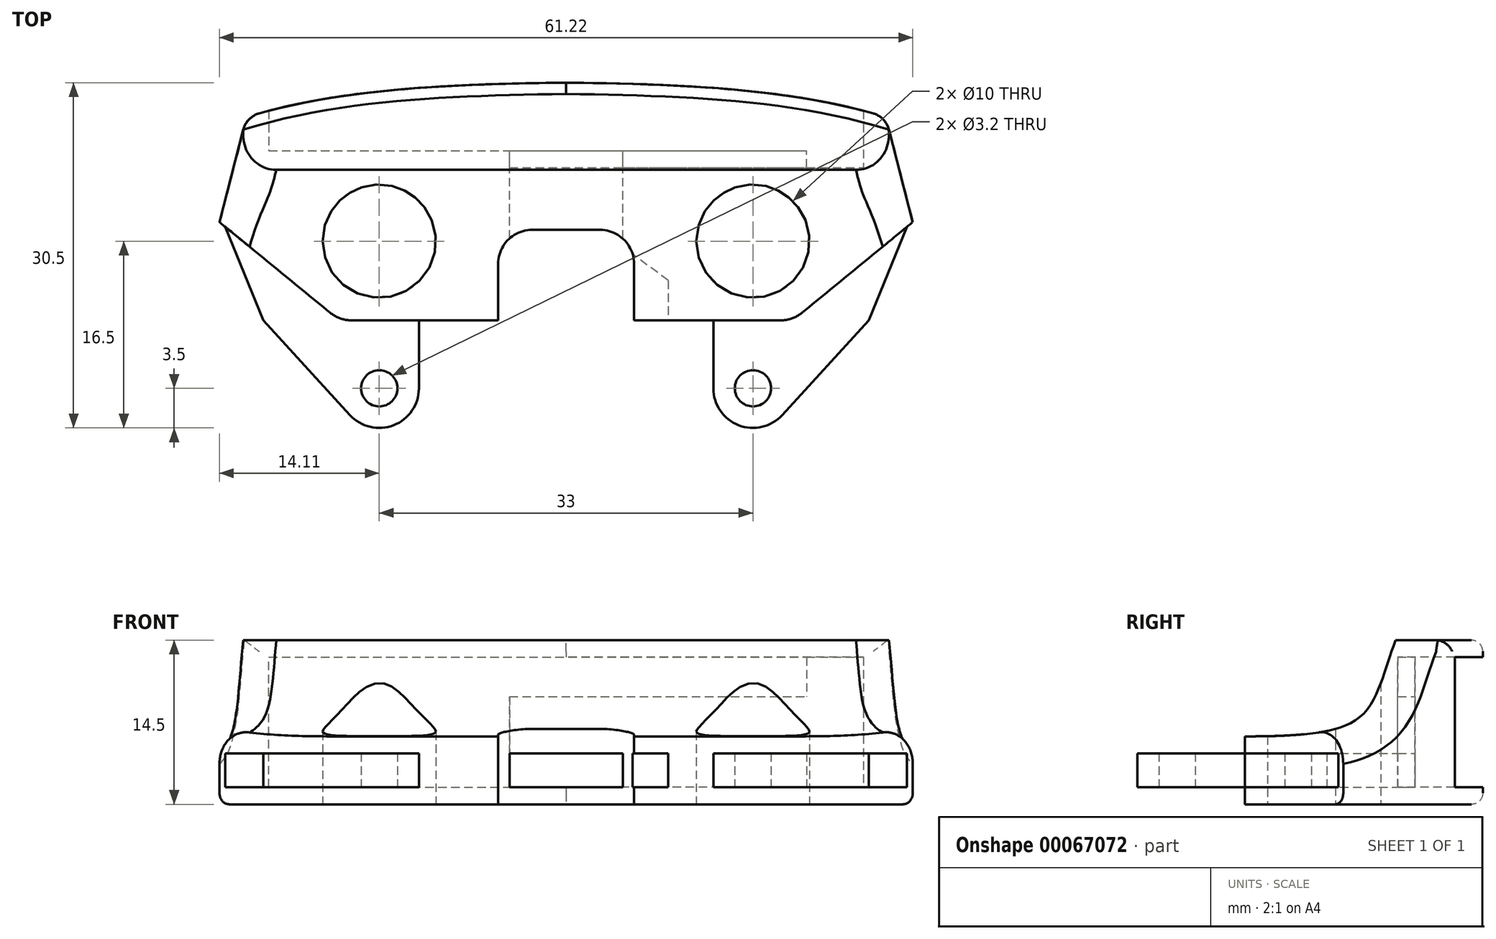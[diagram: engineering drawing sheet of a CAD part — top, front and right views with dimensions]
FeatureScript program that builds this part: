
annotation { "Feature Type Name" : "Feature", "Feature Type Description" : "" }
export const myFeature = defineFeature(function(context is Context, id is Id, definition is map)
    precondition{}
    {
        {
            var Q0;
            Q0=qCreatedBy(makeId("Top.planeOp"),FACE);
            var sketch = newSketch(context, id + "F0", { "sketchPlane" : qUnion([Q0])});
            skLineSegment(sketch, "E0", {"start": v(0, 0) * mm, "end": v(-18.93, 0) * mm});
            skLineSegment(sketch, "E1", {"start": v(-20.83, 0.68) * mm, "end": v(-30.6, 8.68) * mm});
            skLineSegment(sketch, "E2", {"start": v(-30.6, 8.68) * mm, "end": v(-28.5, 16.87) * mm});
            skCircle(sketch, "E3", {"center": v(-16.5, 7) * mm, "radius": 5 * mm});
            skCircle(sketch, "E4", {"center": v(-16.5, -6) * mm, "radius": 1.6 * mm});
            skLineSegment(sketch, "E5", {"start": v(-30.1, 8.26) * mm, "end": v(-26.74, 0) * mm});
            skArc(sketch, "E6", {"start": v(-19.08, -8.36) * mm, "mid": v(-15.23, -9.26) * mm, "end": v(-13, -6) * mm});
            skLineSegment(sketch, "E7", {"start": v(-26.74, 0) * mm, "end": v(-19.08, -8.36) * mm});
            skLineSegment(sketch, "E8", {"start": v(-13, 0) * mm, "end": v(-13, -6) * mm});
            skPoint(sketch, "E9.visualSharp", {"position": v(-20, 0) * mm});
            skArc(sketch, "E9.filletArc", {"start": v(-20.83, 0.68) * mm, "mid": v(-19.94, 0.17) * mm, "end": v(-18.93, 0) * mm});
            skFitSpline(sketch, "E10", {"points": [v(-28.22, 17.97) * mm, v(0, 21) * mm], "startDerivative": vector(21.2, 6.41) * mm, "endDerivative": vector(39.56, 0.4) * mm});
            skArc(sketch, "E11.filletArc", {"start": v(-27.1, 18.3) * mm, "mid": v(-28, 17.77) * mm, "end": v(-28.5, 16.87) * mm});
            skLineSegment(sketch, "E12.MirrorCS", {"start": v(0, 0) * mm, "end": v(18.93, 0) * mm});
            skLineSegment(sketch, "E13.MirrorCS", {"start": v(13, 0) * mm, "end": v(13, -6) * mm});
            skArc(sketch, "E14.MirrorCS", {"start": v(19.08, -8.36) * mm, "mid": v(15.23, -9.26) * mm, "end": v(13, -6) * mm});
            skCircle(sketch, "E15.MirrorC", {"center": v(16.5, -6) * mm, "radius": 1.6 * mm});
            skLineSegment(sketch, "E16.MirrorCS", {"start": v(26.74, 0) * mm, "end": v(19.08, -8.36) * mm});
            skLineSegment(sketch, "E17.MirrorCS", {"start": v(30.1, 8.26) * mm, "end": v(26.74, 0) * mm});
            skArc(sketch, "E18.MirrorCS", {"start": v(20.83, 0.68) * mm, "mid": v(19.94, 0.17) * mm, "end": v(18.93, 0) * mm});
            skLineSegment(sketch, "E19.MirrorCS", {"start": v(20.83, 0.68) * mm, "end": v(30.6, 8.68) * mm});
            skCircle(sketch, "E20.MirrorC", {"center": v(16.5, 7) * mm, "radius": 5 * mm});
            skLineSegment(sketch, "E21.MirrorCS", {"start": v(30.6, 8.68) * mm, "end": v(28.5, 16.87) * mm});
            skArc(sketch, "E22.MirrorCS", {"start": v(27.1, 18.3) * mm, "mid": v(28, 17.77) * mm, "end": v(28.5, 16.87) * mm});
            skFitSpline(sketch, "E23.MirrorCS", {"points": [v(28.22, 17.97) * mm, v(0, 21) * mm], "startDerivative": vector(-21.2, 6.41) * mm, "endDerivative": vector(-39.56, 0.4) * mm});
            skSolve(sketch);
        }
        {
            var Q0;
            {var subQ6=sQuery(id+"F0.wireOp",EDGE,"E2");Q0=makeQuery(id+"F0.imprint","IMPRINT",FACE,{"disambiguationData":[TD([[makeQuery(id+"F0.imprint","IMPRINT",EDGE,{"derivedFrom":subQ6}),-1.0]])]});}
            extrude(context, id + "F1", {"entities" : qUnion([Q0]), "depth" : 14.5 * mm});
        }
        {
            var Q0;
            Q0=makeQuery(id+"F0.imprint","IMPRINT",FACE,{"disambiguationData":[TD([[makeQuery(id+"F0.imprint","IMPRINT",EDGE,{"derivedFrom":sQuery(id+"F0.wireOp",EDGE,"E4")}),-1.0]])]});
            var Q1;
            {var subQ0=sQuery(id+"F0.wireOp",EDGE,"E13.MirrorCS");Q1=makeQuery(id+"F0.imprint","IMPRINT",FACE,{"disambiguationData":[TD([[makeQuery(id+"F0.imprint","IMPRINT",EDGE,{"derivedFrom":subQ0}),1.0]])]});}
            extrude(context, id + "F2", {"entities" : qUnion([Q0, Q1]), "operationType" : NewBodyOperationType.ADD, "depth" : 4.5 * mm, "hasSecondDirection" : true, "secondDirectionOppositeDirection" : false, "secondDirectionDepth" : 1.5 * mm});
        }
        {
            var Q0;
            Q0=qCreatedBy(makeId("Right.planeOp"),FACE);
            var sketch = newSketch(context, id + "F3", { "sketchPlane" : qUnion([Q0])});
            skLineSegment(sketch, "E24", {"start": v(18.3, 14.5) * mm, "end": v(13.3, 14.5) * mm});
            skFitSpline(sketch, "E25", {"points": [v(13.3, 14.5) * mm, v(0, 6) * mm], "startDerivative": vector(-7.24, -20.2) * mm, "endDerivative": vector(-35.3, 0) * mm});
            skLineSegment(sketch, "E26", {"start": v(18.3, 14.5) * mm, "end": v(18.3, 15.71) * mm});
            skLineSegment(sketch, "E27", {"start": v(18.3, 15.71) * mm, "end": v(0, 15.71) * mm});
            skLineSegment(sketch, "E28", {"start": v(0, 15.71) * mm, "end": v(0, 6) * mm});
            skLineSegment(sketch, "E29", {"start": v(0, 4.5) * mm, "end": v(0, 6) * mm, "construction": true});
            skLineSegment(sketch, "E30", {"start": v(21.02, 0) * mm, "end": v(21.02, 6) * mm, "construction": true});
            skSolve(sketch);
        }
        {
            var Q0;
            Q0=makeQuery(id+"F3.imprint","IMPRINT",FACE,{"disambiguationData":[TD([[makeQuery(id+"F3.imprint","IMPRINT",EDGE,{"derivedFrom":sQuery(id+"F3.wireOp",EDGE,"E24")}),-1.0]])]});
            extrude(context, id + "F4", {"entities" : qUnion([Q0]), "operationType" : NewBodyOperationType.REMOVE, "endBound" : BoundingType.SYMMETRIC, "oppositeDirection" : true, "depth" : 80 * mm});
        }
        {
            var Q0;
            Q0=qCreatedBy(makeId("Front.planeOp"),FACE);
            var sketch = newSketch(context, id + "F5", { "sketchPlane" : qUnion([Q0])});
            skLineSegment(sketch, "E31", {"start": v(0, 0) * mm, "end": v(0, 14.5) * mm, "construction": true});
            skLineSegment(sketch, "E32.rect.bottom", {"start": v(-26.25, 1.5) * mm, "end": v(26.25, 1.5) * mm});
            skLineSegment(sketch, "E32.rect.top", {"start": v(-26.25, 13) * mm, "end": v(26.25, 13) * mm});
            skLineSegment(sketch, "E32.rect.left", {"start": v(-26.25, 1.5) * mm, "end": v(-26.25, 13) * mm});
            skLineSegment(sketch, "E32.rect.right", {"start": v(26.25, 1.5) * mm, "end": v(26.25, 13) * mm});
            skPoint(sketch, "E32.rect.middle", {"position": v(0, 7.25) * mm});
            skSolve(sketch);
        }
        {
            var Q0;
            Q0=makeQuery(id+"F5.imprint","IMPRINT",FACE,{"disambiguationData":[TD([[makeQuery(id+"F5.imprint","IMPRINT",EDGE,{"derivedFrom":sQuery(id+"F5.wireOp",EDGE,"E32.rect.bottom")}),1.0]])]});
            extrude(context, id + "F6", {"entities" : qUnion([Q0]), "operationType" : NewBodyOperationType.REMOVE, "oppositeDirection" : true, "depth" : 25 * mm, "hasSecondDirection" : true, "secondDirectionOppositeDirection" : true, "secondDirectionDepth" : 15 * mm});
        }
        {
            var Q0;
            Q0=makeQuery(id+"F6.boolean.opBoolean","COPY",FACE,{"derivedFrom":makeQuery(id+"F6.opExtrude","CAP_FACE",FACE,{"disambiguationData":[OSD([sQuery(id+"F5.wireOp",EDGE,"E32.rect.bottom"),sQuery(id+"F5.wireOp",EDGE,"E32.rect.top"),sQuery(id+"F5.wireOp",EDGE,"E32.rect.left"),sQuery(id+"F5.wireOp",EDGE,"E32.rect.right")])],"isStart":true})});
            var sketch = newSketch(context, id + "F7", { "sketchPlane" : qUnion([Q0])});
            skLineSegment(sketch, "E33", {"start": v(0, 1.5) * mm, "end": v(-5, 1.5) * mm});
            skLineSegment(sketch, "E34", {"start": v(-5, 1.5) * mm, "end": v(-5, 4.5) * mm});
            skLineSegment(sketch, "E35", {"start": v(-5, 4.5) * mm, "end": v(5, 4.5) * mm});
            skLineSegment(sketch, "E36", {"start": v(5, 4.5) * mm, "end": v(5, 1.5) * mm});
            skLineSegment(sketch, "E37", {"start": v(5, 1.5) * mm, "end": v(0, 1.5) * mm});
            skSolve(sketch);
        }
        {
            var Q0;
            Q0=makeQuery(id+"F7.imprint","IMPRINT",FACE,{"disambiguationData":[TD([[makeQuery(id+"F7.imprint","IMPRINT",EDGE,{"derivedFrom":sQuery(id+"F7.wireOp",EDGE,"E33")}),-1.0]])]});
            extrude(context, id + "F8", {"entities" : qUnion([Q0]), "operationType" : NewBodyOperationType.REMOVE, "oppositeDirection" : true, "depth" : 25 * mm});
        }
        {
            var Q0;
            Q0=makeQuery(id+"F6.boolean.opBoolean","COPY",FACE,{"derivedFrom":makeQuery(id+"F6.opExtrude","CAP_FACE",FACE,{"disambiguationData":[OSD([sQuery(id+"F5.wireOp",EDGE,"E32.rect.bottom"),sQuery(id+"F5.wireOp",EDGE,"E32.rect.top"),sQuery(id+"F5.wireOp",EDGE,"E32.rect.left"),sQuery(id+"F5.wireOp",EDGE,"E32.rect.right")])],"isStart":true})});
            var sketch = newSketch(context, id + "F9", { "sketchPlane" : qUnion([Q0])});
            skLineSegment(sketch, "E38", {"start": v(-21.25, 13) * mm, "end": v(-21.25, 1.5) * mm});
            skLineSegment(sketch, "E39", {"start": v(-5, 4.5) * mm, "end": v(-21.25, 4.5) * mm});
            skLineSegment(sketch, "E40", {"start": v(5, 4.5) * mm, "end": v(5, 9.5) * mm});
            skLineSegment(sketch, "E41", {"start": v(5, 9.5) * mm, "end": v(-21.25, 9.5) * mm});
            skSolve(sketch);
        }
        {
            var Q0;
            {var subQ0=sQuery(id+"F5.wireOp",EDGE,"E32.rect.right");var subQ1=makeQuery(id+"F6.boolean.opBoolean","COPY",EDGE,{"derivedFrom":makeQuery(id+"F6.opExtrude","CAP_EDGE",EDGE,{"disambiguationData":[OSD([subQ0])],"isStart":true})});Q0=makeQuery(id+"F9.imprint","IMPRINT",FACE,{"disambiguationData":[TD([[makeQuery(id+"F9.imprint","IMPRINT",EDGE,{"derivedFrom":subQ1}),-1.0]])]});}
            var Q1;
            {var subQ0=sQuery(id+"F9.wireOp",EDGE,"E39");Q1=makeQuery(id+"F9.imprint","IMPRINT",FACE,{"disambiguationData":[TD([[makeQuery(id+"F9.imprint","IMPRINT",EDGE,{"derivedFrom":subQ0}),-1.0]])]});}
            extrude(context, id + "F10", {"entities" : qUnion([Q0, Q1]), "operationType" : NewBodyOperationType.REMOVE, "oppositeDirection" : true, "depth" : 1.5 * mm});
        }
        {
            var Q0;
            Q0=makeQuery(id+"F4.boolean.opBoolean","INTERSECT",EDGE,{"derivedFrom":[makeQuery(id+"F1.opExtrude","SWEPT_FACE",FACE,{"disambiguationData":[OSD([sQuery(id+"F0.wireOp",EDGE,"E2")])]}),makeQuery(id+"F4.opExtrude","SWEPT_FACE",FACE,{"disambiguationData":[OSD([sQuery(id+"F3.wireOp",EDGE,"E25")])]})]});
            var Q1;
            Q1=makeQuery(id+"F4.boolean.opBoolean","INTERSECT",EDGE,{"derivedFrom":[makeQuery(id+"F1.opExtrude","SWEPT_FACE",FACE,{"disambiguationData":[OSD([sQuery(id+"F0.wireOp",EDGE,"E21.MirrorCS")])]}),makeQuery(id+"F4.opExtrude","SWEPT_FACE",FACE,{"disambiguationData":[OSD([sQuery(id+"F3.wireOp",EDGE,"E25")])]})]});
            var Q2;
            Q2=makeQuery(id+"F4.boolean.opBoolean","COPY",EDGE,{"derivedFrom":makeQuery(id+"F4.opExtrude","SWEPT_EDGE",EDGE,{"disambiguationData":[OSD([sQuery(id+"F3.wireOp",EDGE,"E24"),sQuery(id+"F3.wireOp",EDGE,"E25")])]})});
            fillet(context, id + "F11", {"entities" : qUnion([Q0, Q1, Q2]), "radius" : 3 * mm, "tangentPropagation" : true, "allowEdgeOverflow" : false});
        }
        {
            var Q0;
            Q0=makeQuery(id+"F1.opExtrude","CAP_EDGE",EDGE,{"disambiguationData":[OSD([sQuery(id+"F0.wireOp",EDGE,"E10")])],"isStart":false});
            var Q1;
            Q1=makeQuery(id+"F1.opExtrude","CAP_EDGE",EDGE,{"disambiguationData":[OSD([sQuery(id+"F0.wireOp",EDGE,"E23.MirrorCS")])],"isStart":false});
            var Q2;
            Q2=makeQuery(id+"F1.opExtrude","CAP_EDGE",EDGE,{"disambiguationData":[OSD([sQuery(id+"F0.wireOp",EDGE,"E10")])],"isStart":true});
            var Q3;
            Q3=makeQuery(id+"F1.opExtrude","CAP_EDGE",EDGE,{"disambiguationData":[OSD([sQuery(id+"F0.wireOp",EDGE,"E23.MirrorCS")])],"isStart":true});
            fillet(context, id + "F12", {"entities" : qUnion([Q0, Q1, Q2, Q3]), "radius" : 1 * mm, "tangentPropagation" : true, "allowEdgeOverflow" : false});
        }
        {
            var Q0;
            Q0=makeQuery(id+"F1.opExtrude","CAP_FACE",FACE,{"disambiguationData":[OSD([sQuery(id+"F0.wireOp",EDGE,"E0"),sQuery(id+"F0.wireOp",EDGE,"E1"),sQuery(id+"F0.wireOp",EDGE,"E2"),sQuery(id+"F0.wireOp",EDGE,"E3"),sQuery(id+"F0.wireOp",EDGE,"E9.filletArc"),sQuery(id+"F0.wireOp",EDGE,"E10"),sQuery(id+"F0.wireOp",EDGE,"E11.filletArc"),sQuery(id+"F0.wireOp",EDGE,"E12.MirrorCS"),sQuery(id+"F0.wireOp",EDGE,"E18.MirrorCS"),sQuery(id+"F0.wireOp",EDGE,"E19.MirrorCS"),sQuery(id+"F0.wireOp",EDGE,"E20.MirrorC"),sQuery(id+"F0.wireOp",EDGE,"E21.MirrorCS"),sQuery(id+"F0.wireOp",EDGE,"E22.MirrorCS"),sQuery(id+"F0.wireOp",EDGE,"E23.MirrorCS")])],"isStart":true});
            var sketch = newSketch(context, id + "F13", { "sketchPlane" : qUnion([Q0])});
            skLineSegment(sketch, "E42.bottom", {"start": v(-6, 0) * mm, "end": v(6, 0) * mm});
            skLineSegment(sketch, "E42.top", {"start": v(-3, -8) * mm, "end": v(3, -8) * mm});
            skLineSegment(sketch, "E42.left", {"start": v(-6, 0) * mm, "end": v(-6, -5) * mm});
            skLineSegment(sketch, "E42.right", {"start": v(6, 0) * mm, "end": v(6, -5) * mm});
            skPoint(sketch, "E43.visualSharp", {"position": v(-6, -8) * mm});
            skArc(sketch, "E43.filletArc", {"start": v(-6, -5) * mm, "mid": v(-5.12, -7.12) * mm, "end": v(-3, -8) * mm});
            skPoint(sketch, "E44.visualSharp", {"position": v(6, -8) * mm});
            skArc(sketch, "E44.filletArc", {"start": v(3, -8) * mm, "mid": v(5.12, -7.12) * mm, "end": v(6, -5) * mm});
            skSolve(sketch);
        }
        {
            var Q0;
            Q0=makeQuery(id+"F13.imprint","IMPRINT",FACE,{"disambiguationData":[TD([[makeQuery(id+"F13.imprint","IMPRINT",EDGE,{"derivedFrom":sQuery(id+"F13.wireOp",EDGE,"E42.bottom")}),1.0]])]});
            extrude(context, id + "F14", {"entities" : qUnion([Q0]), "operationType" : NewBodyOperationType.REMOVE, "oppositeDirection" : true, "depth" : 25 * mm});
        }
        {
            var Q0;
            {var subQ1=sQuery(id+"F0.wireOp",EDGE,"E18.MirrorCS");var subQ7=sQuery(id+"F0.wireOp",EDGE,"E12.MirrorCS");var subQ8=sQuery(id+"F0.wireOp",EDGE,"E0");Q0=makeQuery(id+"F14.boolean.opBoolean","SPLIT",FACE,{"disambiguationData":[TD([makeQuery(id+"F1.opExtrude","SWEPT_FACE",FACE,{"disambiguationData":[OSD([subQ1])]})])],"derivedFrom":makeQuery(id+"F1.opExtrude","SWEPT_FACE",FACE,{"disambiguationData":[OSD([subQ8,subQ7])]})});}
            var sketch = newSketch(context, id + "F15", { "sketchPlane" : qUnion([Q0])});
            skLineSegment(sketch, "E45.bottom", {"start": v(5, 1.5) * mm, "end": v(9, 1.5) * mm});
            skLineSegment(sketch, "E45.top", {"start": v(5, 4.5) * mm, "end": v(9, 4.5) * mm});
            skLineSegment(sketch, "E45.left", {"start": v(5, 1.5) * mm, "end": v(5, 4.5) * mm});
            skLineSegment(sketch, "E45.right", {"start": v(9, 1.5) * mm, "end": v(9, 4.5) * mm});
            skSolve(sketch);
        }
        {
            var Q0;
            Q0=makeQuery(id+"F15.imprint","IMPRINT",FACE,{"disambiguationData":[TD([[makeQuery(id+"F15.imprint","IMPRINT",EDGE,{"derivedFrom":sQuery(id+"F15.wireOp",EDGE,"E45.bottom")}),1.0]])]});
            extrude(context, id + "F16", {"entities" : qUnion([Q0]), "operationType" : NewBodyOperationType.REMOVE, "oppositeDirection" : true, "depth" : 3 * mm});
        }
        {
            var Q0;
            Q0=makeQuery(id+"F16.boolean.opBoolean","INTERSECT",EDGE,{"derivedFrom":[makeQuery(id+"F14.boolean.opBoolean","COPY",FACE,{"derivedFrom":makeQuery(id+"F14.opExtrude","SWEPT_FACE",FACE,{"disambiguationData":[OSD([sQuery(id+"F13.wireOp",EDGE,"E42.right")])]})}),makeQuery(id+"F16.opExtrude","CAP_FACE",FACE,{"disambiguationData":[OSD([sQuery(id+"F15.wireOp",EDGE,"E45.bottom"),sQuery(id+"F15.wireOp",EDGE,"E45.top"),sQuery(id+"F15.wireOp",EDGE,"E45.left"),sQuery(id+"F15.wireOp",EDGE,"E45.right")])],"isStart":false})]});
            chamfer(context, id + "F17", {"entities" : qUnion([Q0]), "width" : 4 * mm, "tangentPropagation" : true});
        }
    });
